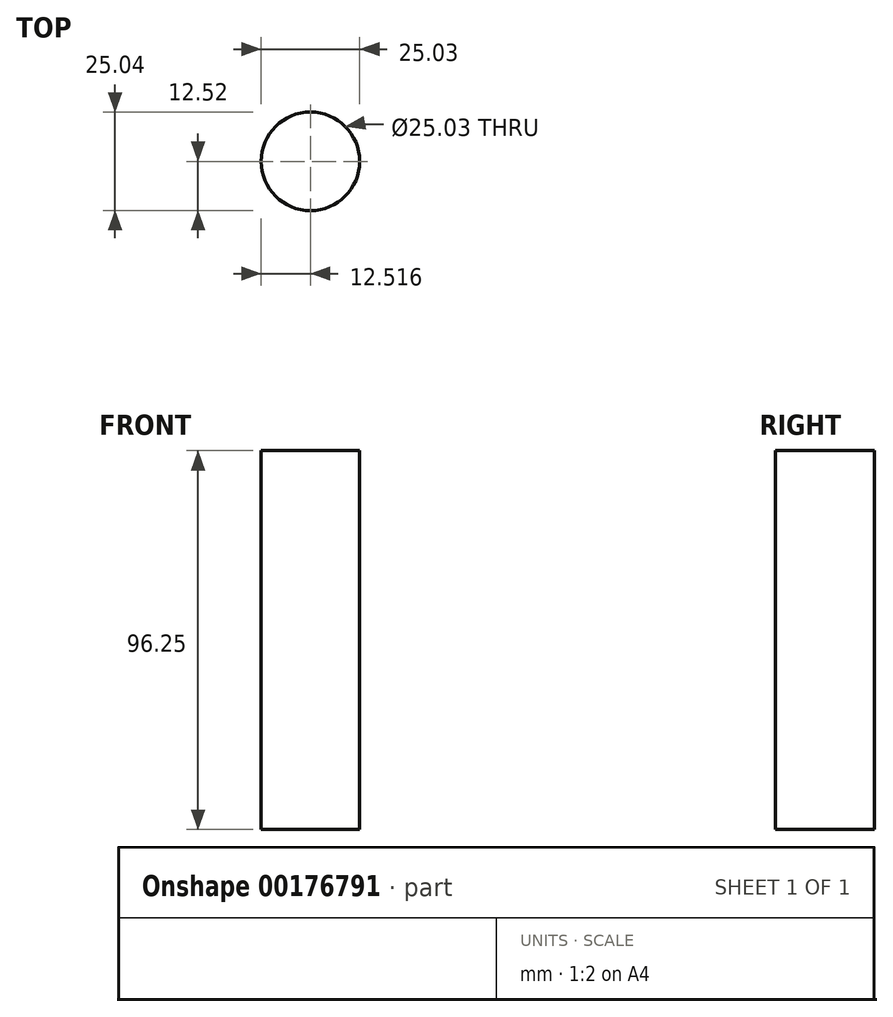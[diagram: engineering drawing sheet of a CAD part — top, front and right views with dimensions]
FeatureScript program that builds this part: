
annotation { "Feature Type Name" : "Feature", "Feature Type Description" : "" }
export const myFeature = defineFeature(function(context is Context, id is Id, definition is map)
    precondition{}
    {
        {
            var Q0;
            Q0=qCreatedBy(makeId("Front.planeOp"),FACE);
            var sketch = newSketch(context, id + "F0", { "sketchPlane" : qUnion([Q0])});
            skLineSegment(sketch, "E0", {"start": v(-36.5, 53.79) * mm, "end": v(-36.5, -43.06) * mm});
            skLineSegment(sketch, "E1", {"start": v(-23.99, 53.79) * mm, "end": v(-23.99, -42.46) * mm});
            skArc(sketch, "E2", {"start": v(-23.99, -44.85) * mm, "mid": v(-8.38, 4.47) * mm, "end": v(-23.99, 53.79) * mm});
            skSolve(sketch);
        }
        {
            var Q0;
            Q0=sQuery(id+"F0.wireOp",EDGE,"E1");
            var Q1;
            Q1=sQuery(id+"F0.wireOp",EDGE,"E0");
            revolve(context, id + "F1", {"bodyType" : ToolBodyType.SURFACE, "surfaceEntities" : qUnion([Q0]), "axis" : qUnion([Q1]), "revolveType" : RevolveType.FULL});
        }
    });
